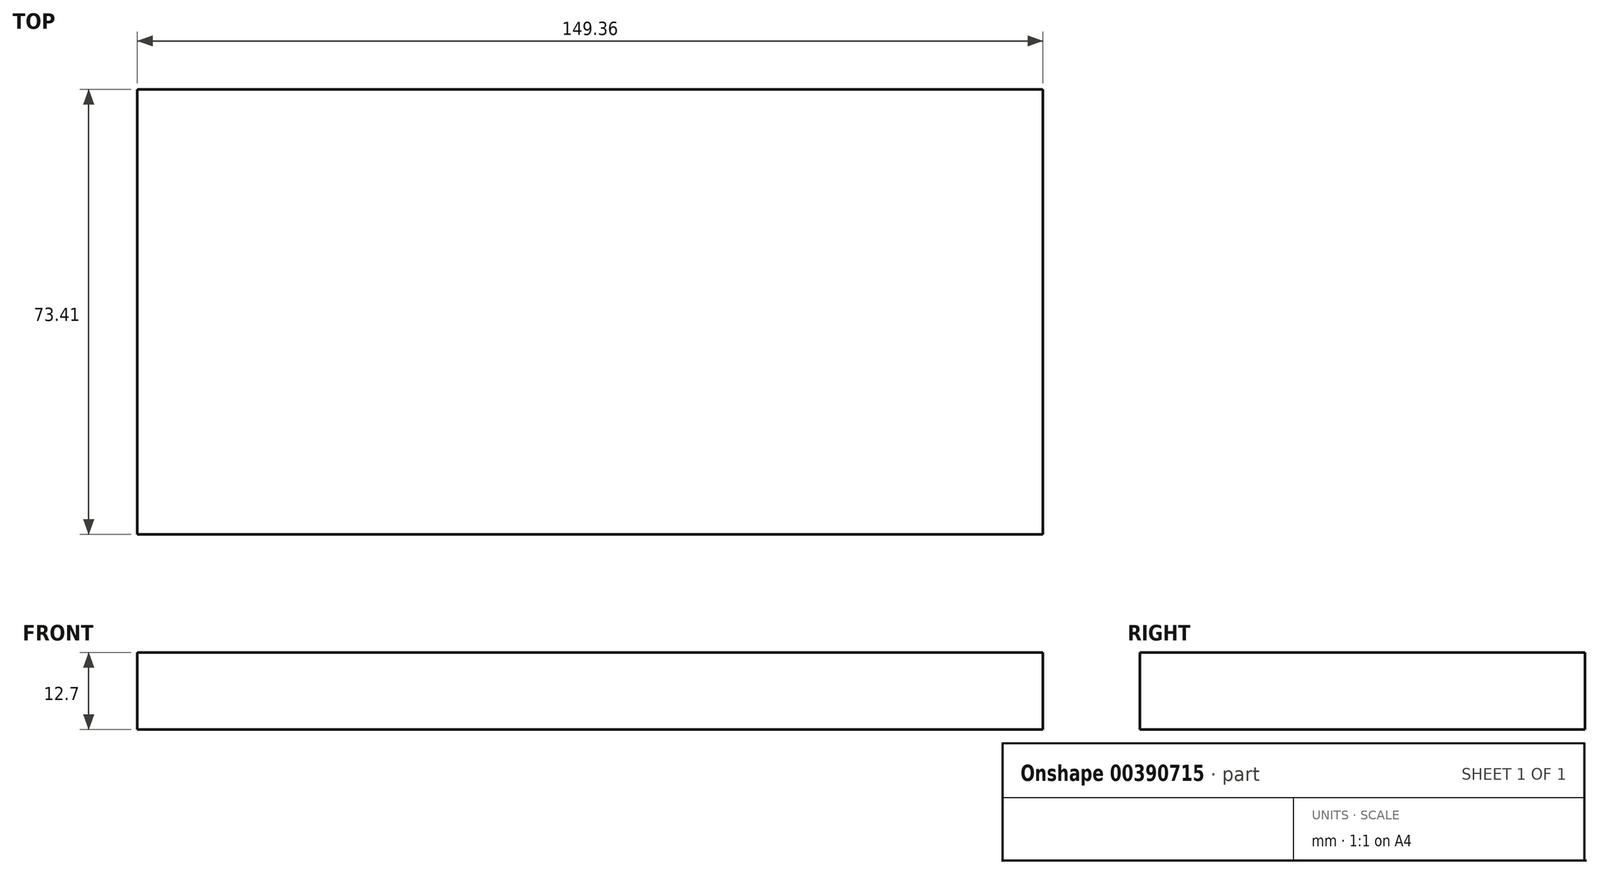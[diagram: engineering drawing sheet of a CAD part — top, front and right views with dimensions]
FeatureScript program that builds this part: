
annotation { "Feature Type Name" : "Feature", "Feature Type Description" : "" }
export const myFeature = defineFeature(function(context is Context, id is Id, definition is map)
    precondition{}
    {
        {
            var Q0;
            Q0=qCreatedBy(makeId("Top.planeOp"),FACE);
            var sketch = newSketch(context, id + "F0", { "sketchPlane" : qUnion([Q0])});
            skLineSegment(sketch, "E0.bottom", {"start": v(-136.78, 5.66) * mm, "end": v(12.58, 5.66) * mm});
            skLineSegment(sketch, "E0.top", {"start": v(-136.78, -67.75) * mm, "end": v(12.58, -67.75) * mm});
            skLineSegment(sketch, "E0.left", {"start": v(-136.78, 5.66) * mm, "end": v(-136.78, -67.75) * mm});
            skLineSegment(sketch, "E0.right", {"start": v(12.58, 5.66) * mm, "end": v(12.58, -67.75) * mm});
            skSolve(sketch);
        }
        {
            var Q0;
            Q0 = qSketchRegion(id + "F0", true);
            extrude(context, id + "F1", {"entities" : qUnion([Q0]), "depth" : 12.7 * mm});
        }
    });
